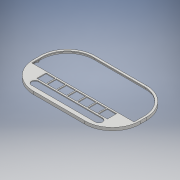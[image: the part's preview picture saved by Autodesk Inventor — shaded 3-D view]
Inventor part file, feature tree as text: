
AUTODESK INVENTOR PART (.ipt)
format: ipt  version: 2018 (Build 220112000, 112)  size: 217,600 bytes
history: native  units: mm
features: extrude x3, sketch x2, mirror x1, projected_geometry x1
ambient origin geometry x8: Origin, YZ Plane, XZ Plane, XY Plane, X Axis, Y Axis, Z Axis, Center Point
bodies: Solid1 (feature_tree)
feature tree (7):
  sketch  "Sketch1"  dims[d0=104.0mm d1=60.0mm]
  extrude  "Extrusion1"  Depth=60.0mm
  extrude  "Extrusion2"  Depth=58.2mm
  extrude  "Extrusion3"  Depth=2.0mm
  mirror  "Mirror1"
  sketch  "Sketch2"  dims[d2=27.0mm d3=58.2mm d4=2.0mm d5=23.0mm d6=9.0mm d7=70.0mm d9=10.0mm d10=10.0mm d12=10.0mm d16=62.5mm d17=7.0mm d20=2.1mm d21=0.0mm d22=0.8mm d23=0.0mm d24=13.0mm d25=22.5mm d26=1.0mm d27=120.0deg d28=10.0mm d29=0.0mm]
  projected_geometry  "Projected Loop1"
